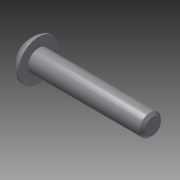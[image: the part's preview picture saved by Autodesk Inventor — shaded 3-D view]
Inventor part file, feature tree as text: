
AUTODESK INVENTOR PART (.ipt)
format: ipt  version: 2015 (Build 190159000, 159)  size: 123,904 bytes
history: native  units: in
note: dims shown in document units (in); Inventor stores cm internally (conversion verified against a paired STEP export)
features: other x3, extrude x1, chamfer x1, imported_body x1, sketch x1
ambient origin geometry x8: Origin, YZ Plane, XZ Plane, XY Plane, X Axis, Y Axis, Z Axis, Center Point
bodies: Body1 (feature_tree)
feature tree (7):
  other  "Bolt 0.875 inch"
  parser-record x1  (decoder bookkeeping rows leaked as tree rows — omitted from the tree; the rows remain in map.json)
  other  "Bolt"
  extrude  "thread length"  Depth=0.875in TaperAngle=0.0deg
  chamfer  "thread chamfer"  Distance=0.02in Angle=45.0deg
  imported_body  "Base1"
  sketch  "Sketch1"  dims[d0=0.164in d1=0.875in d2=0.0in d3=0.02in d4=0.125in d5=45.0deg d7=0.0in d9=0.0in]
